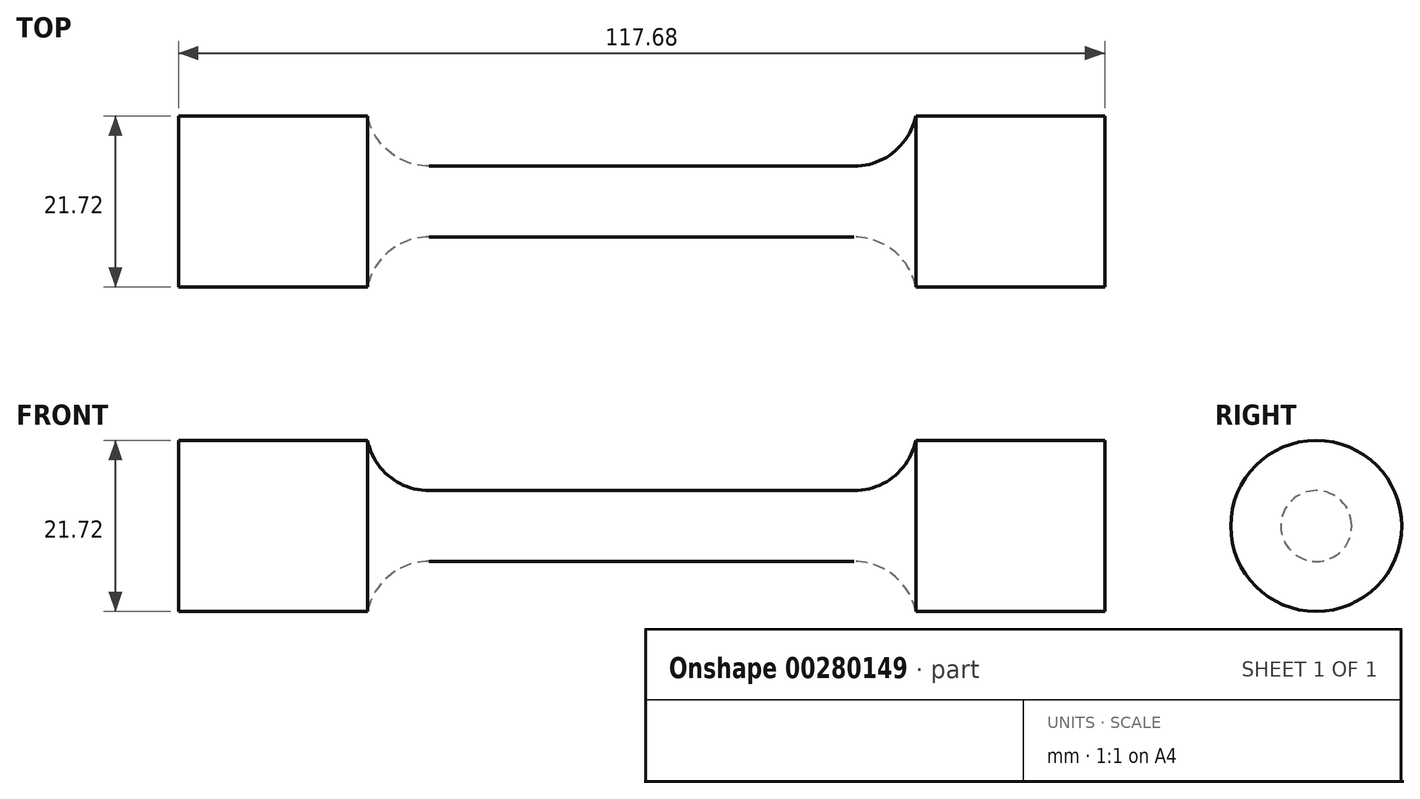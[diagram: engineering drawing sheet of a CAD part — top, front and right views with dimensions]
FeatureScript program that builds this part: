
annotation { "Feature Type Name" : "Feature", "Feature Type Description" : "" }
export const myFeature = defineFeature(function(context is Context, id is Id, definition is map)
    precondition{}
    {
        {
            var Q0;
            Q0=qCreatedBy(makeId("Front.planeOp"),FACE);
            var sketch = newSketch(context, id + "F0", { "sketchPlane" : qUnion([Q0])});
            skLineSegment(sketch, "E0", {"start": v(0, 4.5) * mm, "end": v(27, 4.5) * mm});
            skArc(sketch, "E1", {"start": v(27, 4.5) * mm, "mid": v(32.04, 6.3) * mm, "end": v(34.83, 10.86) * mm});
            skLineSegment(sketch, "E2", {"start": v(34.83, 10.86) * mm, "end": v(58.84, 10.86) * mm});
            skLineSegment(sketch, "E3", {"start": v(58.84, 10.86) * mm, "end": v(58.84, 0) * mm});
            skLineSegment(sketch, "E4.MirrorCS", {"start": v(-58.84, 10.86) * mm, "end": v(-58.84, 0) * mm});
            skArc(sketch, "E5.MirrorCS", {"start": v(-27, 4.5) * mm, "mid": v(-32.04, 6.3) * mm, "end": v(-34.83, 10.86) * mm});
            skLineSegment(sketch, "E6.MirrorCS", {"start": v(-34.83, 10.86) * mm, "end": v(-58.84, 10.86) * mm});
            skLineSegment(sketch, "E7.MirrorCS", {"start": v(0, 4.5) * mm, "end": v(-27, 4.5) * mm});
            skLineSegment(sketch, "E8", {"start": v(-58.84, 0) * mm, "end": v(58.84, 0) * mm});
            skSolve(sketch);
        }
        {
            var Q0;
            Q0 = qSketchRegion(id + "F0", true);
            var Q1;
            Q1=sQuery(id+"F0.wireOp",EDGE,"E8");
            revolve(context, id + "F1", {"entities" : qUnion([Q0]), "axis" : qUnion([Q1]), "revolveType" : RevolveType.FULL});
        }
    });
